# Revit family: QPTW (HWC on Induction Port)
name_source: partatom
category: Mechanical Equipment
revit_build: Autodesk Revit 2016 (Build: 20150714_1515(x64)
units: mm (PartAtom-declared; Revit-internal decimal feet)

## family parameters
Always vertical = Yes
Cut with Voids When Loaded = No
Part Type = Normal
Room Calculation Point = No
Round Connector Dimension = Use Radius
Shared = No
Work Plane-Based = No

## types (26) — shared parameters
Description = Series Fan Powered Air Terminal with Hot Water Coil
HWC Conn = 1"
HWC Conn "D" = 15/16"
HWC Conn "E" = 1 37/64"
HWC Depth 1-Row "Z" = 12 1/4"
Manufacturer = Anemostat
Model = QPTW
URL = http://www.anemostat.com

## per-type parameters (varying)
| type | Diameter | Discharge "Z" | Discharge Height "Y" | Discharge Width "X" | Duct Inlet Radius | HWC Conn "B" | HWC Conn "C" | HWC Conn Top | Height | Induction Height "D" | Induction Width "C" | Length | Radius | Width |
| 11706 QPTW 1/6-hp - 06" (IP) | 5 7/8" | 3" | 11" | 11 1/2" | 3" | 3 3/8" | 1 39/64" | 10 1/16" | 15" | 15" | 16" | 30" | 2 15/16" | 34" |
| 11707 QPTW 1/6-hp - 07" (IP) | 6 7/8" | 3" | 11" | 11 1/2" | 3" | 3 3/8" | 1 39/64" | 10 1/16" | 15" | 15" | 16" | 30" | 3 7/16" | 34" |
| 11708 QPTW 1/6-hp - 08" (IP) | 7 7/8" | 3" | 11" | 11 1/2" | 4" | 3 3/8" | 1 39/64" | 10 1/16" | 15" | 15" | 16" | 30" | 3 15/16" | 34" |
| 12508 QPTW 1/4-hp - 08" (IP) | 7 7/8" | 3" | 11" | 11 1/2" | 4" | 3 25/64" | 1 5/8" | 10 1/16" | 15" | 15" | 16" | 30" | 3 15/16" | 34" |
| 12509 QPTW 1/4-hp - 09" (IP) | 8 7/8" | 3" | 11" | 11 1/2" | 4" | 3 25/64" | 1 5/8" | 10 1/16" | 15" | 15" | 16" | 30" | 4 7/16" | 34" |
| 11709 QPTW 1/6-hp - 09" (IP) | 8 7/8" | 3" | 11" | 11 1/2" | 4" | 3 3/8" | 1 39/64" | 10 1/16" | 15" | 15" | 16" | 30" | 4 7/16" | 34" |
| 12506 QPTW 1/4-hp - 06" (IP) | 5 7/8" | 3" | 11" | 11 1/2" | 3" | 3 25/64" | 1 5/8" | 10 1/16" | 15" | 15" | 16" | 30" | 2 15/16" | 34" |
| 12507 QPTW 1/4-hp - 07" (IP) | 6 7/8" | 3" | 11" | 11 1/2" | 3" | 3 25/64" | 1 5/8" | 10 1/16" | 15" | 15" | 16" | 30" | 3 7/16" | 34" |
| 21709 QPTW 1/6-hp - 09" (IP) | 8 7/8" | 3" | 12" | 14" | 4" | 3 3/8" | 1 39/64" | 11 1/16" | 18" | 17 1/2" | 20" | 34" | 4 7/16" | 40" |
| 21710 QPTW 1/6-hp - 10" (IP) | 9 7/8" | 3" | 12" | 14" | 5" | 3 3/8" | 1 39/64" | 11 1/16" | 18" | 17 1/2" | 20" | 34" | 4 15/16" | 40" |
| 21712 QPTW 1/6-hp - 12" (IP) | 11 7/8" | 3" | 12" | 14" | 6" | 3 3/8" | 1 39/64" | 11 1/16" | 18" | 17 1/2" | 20" | 34" | 5 15/16" | 40" |
| 22509 QPTW 1/4-hp - 09" (IP) | 8 7/8" | 3" | 12" | 14" | 4" | 3 3/8" | 1 39/64" | 11 1/16" | 18" | 17 1/2" | 20" | 34" | 4 7/16" | 40" |
| 22510 QPTW 1/4-hp - 10" (IP) | 9 7/8" | 3" | 12" | 14" | 5" | 3 3/8" | 1 39/64" | 11 1/16" | 18" | 17 1/2" | 20" | 34" | 4 15/16" | 40" |
| 22512 QPTW 1/4-hp - 12" (IP) | 11 7/8" | 3" | 12" | 14" | 6" | 3 3/8" | 1 39/64" | 11 1/16" | 18" | 17 1/2" | 20" | 34" | 5 15/16" | 40" |
| 25009 QPTW 1/2-hp - 09" (IP) | 8 7/8" | 3" | 12" | 14" | 4" | 3 3/8" | 1 39/64" | 11 1/16" | 18" | 17 1/2" | 20" | 34" | 4 7/16" | 40" |
| 25010 QPTW 1/2-hp - 10" (IP) | 9 7/8" | 3" | 12" | 14" | 5" | 3 3/8" | 1 39/64" | 11 1/16" | 18" | 17 1/2" | 20" | 34" | 4 15/16" | 40" |
| 25012 QPTW 1/2-hp - 12" (IP) | 11 7/8" | 3" | 12" | 14" | 6" | 3 3/8" | 1 39/64" | 11 1/16" | 18" | 17 1/2" | 20" | 34" | 5 15/16" | 40" |
| 35012 QPTW 1/2-hp - 12" (IP) | 11 7/8" | 2 1/4" | 16" | 19" | 6" | 3 3/8" | 1 39/64" | 15 1/16" | 20" | 17 1/2" | 24" | 40" | 5 15/16" | 46" |
| 35014 QPTW 1/2-hp - 14" (IP) | 13 7/8" | 2 1/4" | 16" | 19" | 7" | 3 3/8" | 1 39/64" | 15 1/16" | 20" | 17 1/2" | 24" | 40" | 6 15/16" | 46" |
| 35016 QPTW 1/2-hp - 16" (IP) | 15 7/8" | 2 1/4" | 16" | 19" | 8" | 3 3/8" | 1 39/64" | 15 1/16" | 20" | 17 1/2" | 24" | 40" | 7 15/16" | 46" |
| 37512 QPTW 3/4-hp - 12" (IP) | 11 7/8" | 2 1/4" | 16" | 19" | 6" | 3 3/8" | 1 39/64" | 15 1/16" | 20" | 17 1/2" | 24" | 40" | 5 15/16" | 46" |
| 37514 QPTW 3/4-hp - 14" (IP) | 13 7/8" | 2 1/4" | 16" | 19" | 7" | 3 3/8" | 1 39/64" | 15 1/16" | 20" | 17 1/2" | 24" | 40" | 6 15/16" | 46" |
| 37516 QPTW 3/4-hp - 16" (IP) | 15 7/8" | 2 1/4" | 16" | 19" | 8" | 3 3/8" | 1 39/64" | 15 1/16" | 20" | 17 1/2" | 24" | 40" | 7 15/16" | 46" |
| 31012 QPTW 1-hp - 12" (IP) | 11 7/8" | 2 1/4" | 16" | 19" | 6" | 3 3/8" | 1 39/64" | 15 1/16" | 20" | 17 1/2" | 24" | 40" | 5 15/16" | 46" |
| 31014 QPTW 1-hp - 14" (IP) | 13 7/8" | 2 1/4" | 16" | 19" | 7" | 3 3/8" | 1 39/64" | 15 1/16" | 20" | 17 1/2" | 24" | 40" | 6 15/16" | 46" |
| 31016 QPTW 1-hp - 16" (IP) | 15 7/8" | 2 1/4" | 16" | 19" | 8" | 3 3/8" | 1 39/64" | 15 1/16" | 20" | 17 1/2" | 24" | 40" | 7 15/16" | 46" |

## geometry (parser evidence)
native form markers: Sweep x3
no freeform markers — native parametric forms only
